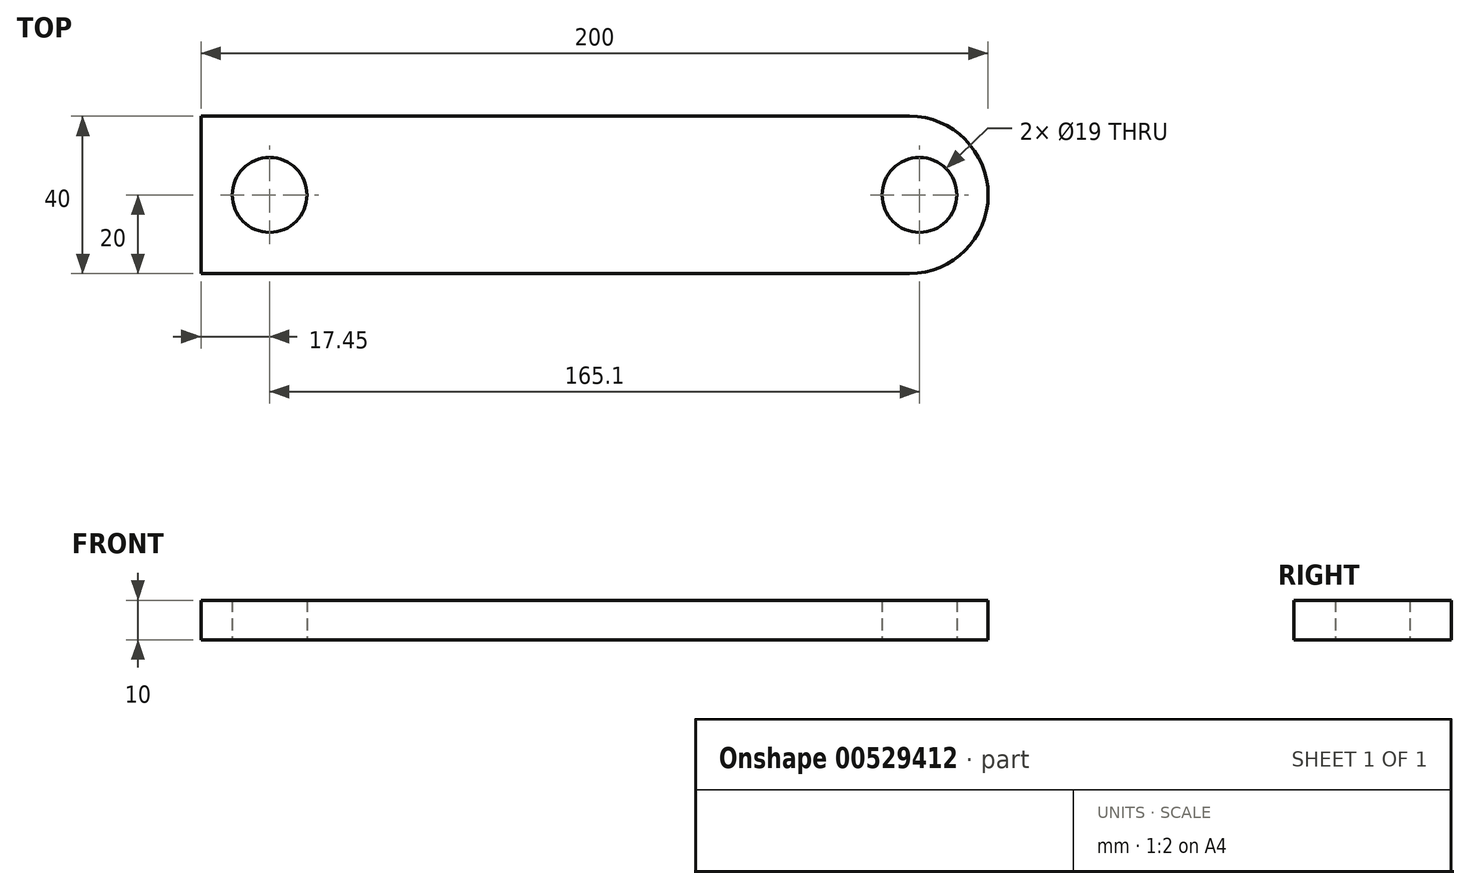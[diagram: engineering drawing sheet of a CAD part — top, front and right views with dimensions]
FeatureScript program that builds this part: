
annotation { "Feature Type Name" : "Feature", "Feature Type Description" : "" }
export const myFeature = defineFeature(function(context is Context, id is Id, definition is map)
    precondition{}
    {
        {
            var Q0;
            Q0=qCreatedBy(makeId("Top.planeOp"),FACE);
            var sketch = newSketch(context, id + "F0", { "sketchPlane" : qUnion([Q0])});
            skLineSegment(sketch, "E0.bottom", {"start": v(80, -20) * mm, "end": v(-100, -20) * mm});
            skLineSegment(sketch, "E0.top", {"start": v(80, 20) * mm, "end": v(-100, 20) * mm});
            skLineSegment(sketch, "E0.left", {"start": v(100, 0) * mm, "end": v(100, 0) * mm});
            skLineSegment(sketch, "E0.right", {"start": v(-100, -20) * mm, "end": v(-100, 20) * mm});
            skPoint(sketch, "E0.middle", {"position": v(0, 0) * mm});
            skLineSegment(sketch, "E1", {"start": v(0, 0) * mm, "end": v(82.55, 0) * mm, "construction": true});
            skLineSegment(sketch, "E2", {"start": v(0, 0) * mm, "end": v(-82.55, 0) * mm, "construction": true});
            skCircle(sketch, "E3", {"center": v(82.55, 0) * mm, "radius": 9.5 * mm});
            skCircle(sketch, "E4", {"center": v(-82.55, 0) * mm, "radius": 9.5 * mm});
            skPoint(sketch, "E5.visualSharp", {"position": v(100, 20) * mm});
            skArc(sketch, "E5.filletArc", {"start": v(100, 0) * mm, "mid": v(94.14, 14.14) * mm, "end": v(80, 20) * mm});
            skPoint(sketch, "E6.visualSharp", {"position": v(100, -20) * mm});
            skArc(sketch, "E6.filletArc", {"start": v(80, -20) * mm, "mid": v(94.14, -14.14) * mm, "end": v(100, 0) * mm});
            skSolve(sketch);
        }
        {
            var Q0;
            {var subQ0=sQuery(id+"F0.wireOp",EDGE,"E0.right");Q0=makeQuery(id+"F0.imprint","IMPRINT",FACE,{"disambiguationData":[TD([[makeQuery(id+"F0.imprint","IMPRINT",EDGE,{"derivedFrom":subQ0}),-1.0]])]});}
            extrude(context, id + "F1", {"entities" : qUnion([Q0]), "depth" : 10 * mm, "offsetDistance" : 25 * mm});
        }
    });
